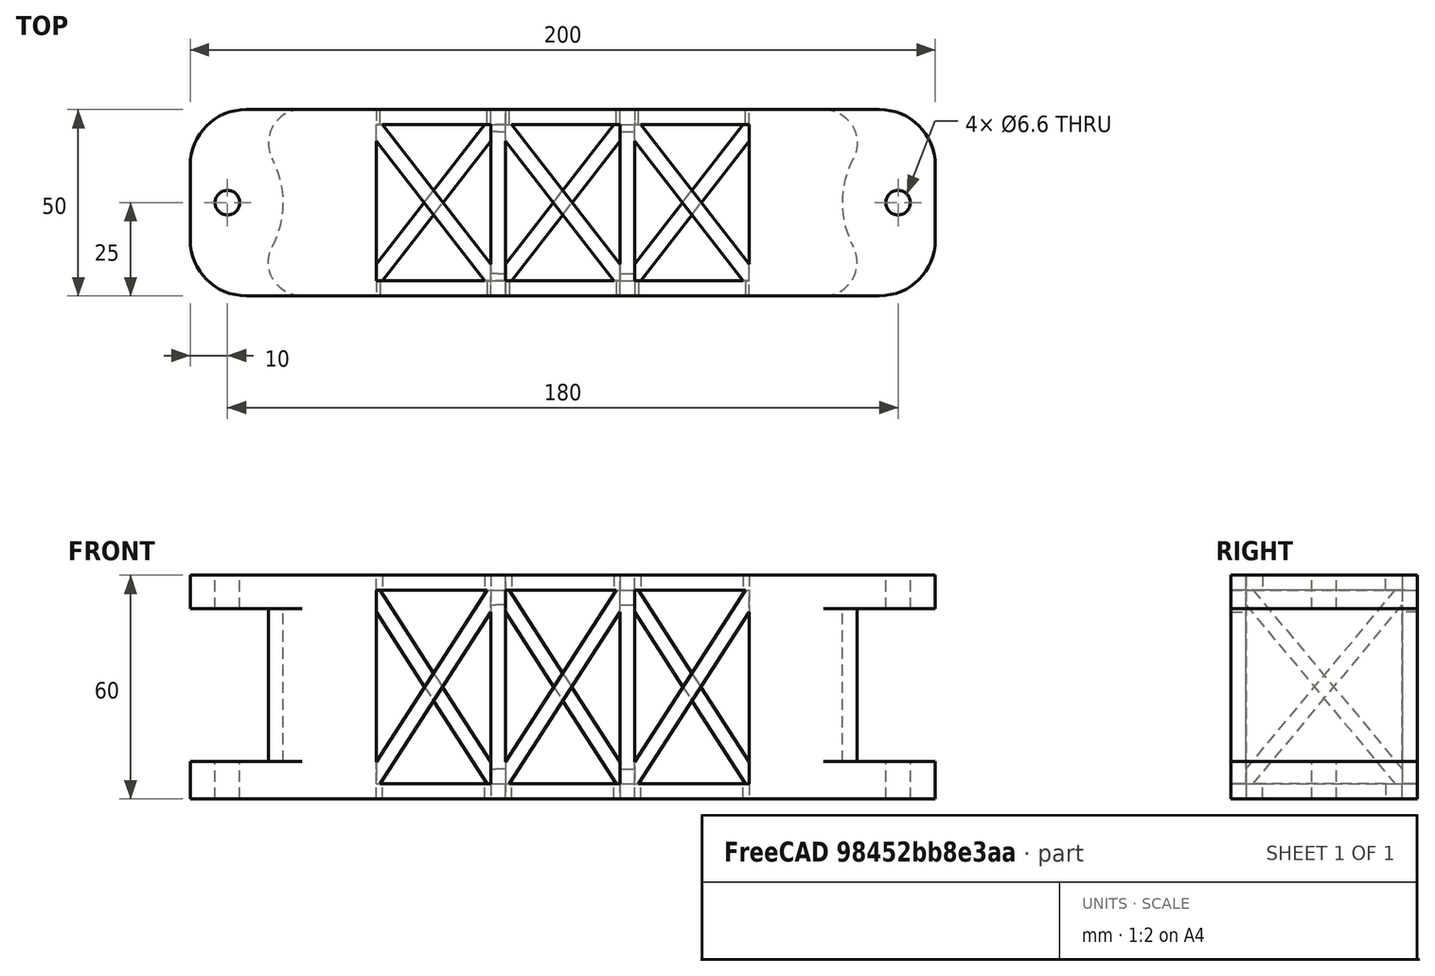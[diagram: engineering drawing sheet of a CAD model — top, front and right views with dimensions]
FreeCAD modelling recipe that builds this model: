
FCSTD DOCUMENT  (FreeCAD 0.19R24291 (Git))
Label: webcam-arm
License: Other
LicenseURL: https://www.gnu.org/licenses/gpl-3.0.en.html
objects: Part::Fillet×4, Part::Box×2, Part::MultiFuse×2, Part::Cut×2, Part::Cylinder×2, Part::Feature×1, Part::Mirroring×1
note: 14 computed .brp shape members not serialized (recipe doc carries the construction recipe); baked Part::Feature solids carry a one-line shape summary decoded from their .brp

FEATURE [Part::Feature] Shape
  shape: bbox 200 x 50 x 60 mm, 384 faces (baked)
FEATURE [Part::Box] Box  label="Cube"
  AttacherType = Attacher::AttachEngine3D
  Height = 41
  Length = 50
  Placement = pos=(3.6e-15,-10.3553,10) rot=(0,0,1;0.785398rad)
  Width = 50
FEATURE [Part::Fillet] Fillet
  Base = -> Box
  Edges = 1 edges r=25: [Edge5]
FEATURE [Part::Box] Box001  label="Cube001"
  AttacherType = Attacher::AttachEngine3D
  Height = 41
  Length = 50
  Placement = pos=(4e-15,-10.3553,10) rot=(0,0,1;0.785398rad)
  Width = 50
FEATURE [Part::Fillet] Fillet001
  Base = -> Box001
  Edges = 1 edges r=25: [Edge5]
FEATURE [Part::Mirroring] Part__Mirroring  label="Fillet001 (Mirror #1)"
  Base = (100,0,0)
  Normal = (1,0,0)
  Source = -> Fillet001
FEATURE [Part::MultiFuse] Fusion
  Shapes = -> [Fillet,Part__Mirroring]
FEATURE [Part::Cut] Cut
  Base = -> Shape
  Tool = -> Fusion
FEATURE [Part::Fillet] Fillet002
  Base = -> Cut
  Edges = 4 edges r=9: [Edge54,Edge210,Edge882,Edge941]
FEATURE [Part::Fillet] Fillet003
  Base = -> Fillet002
  Edges = 8 edges r=15: [Edge3,Edge14,Edge26,Edge45,Edge922,Edge926,Edge938,Edge939]
FEATURE [Part::Cylinder] Cylinder
  Angle = 360
  AttacherType = Attacher::AttachEngine3D
  Height = 70
  Placement = pos=(10,25,-1) rot=(0,0,1;0rad)
  Radius = 3.3
FEATURE [Part::Cylinder] Cylinder001
  Angle = 360
  AttacherType = Attacher::AttachEngine3D
  Height = 70
  Placement = pos=(190,25,-1) rot=(0,0,1;0rad)
  Radius = 3.3
FEATURE [Part::MultiFuse] Fusion001
  Shapes = -> [Cylinder,Cylinder001]
FEATURE [Part::Cut] Cut001
  Base = -> Fillet003
  Tool = -> Fusion001
